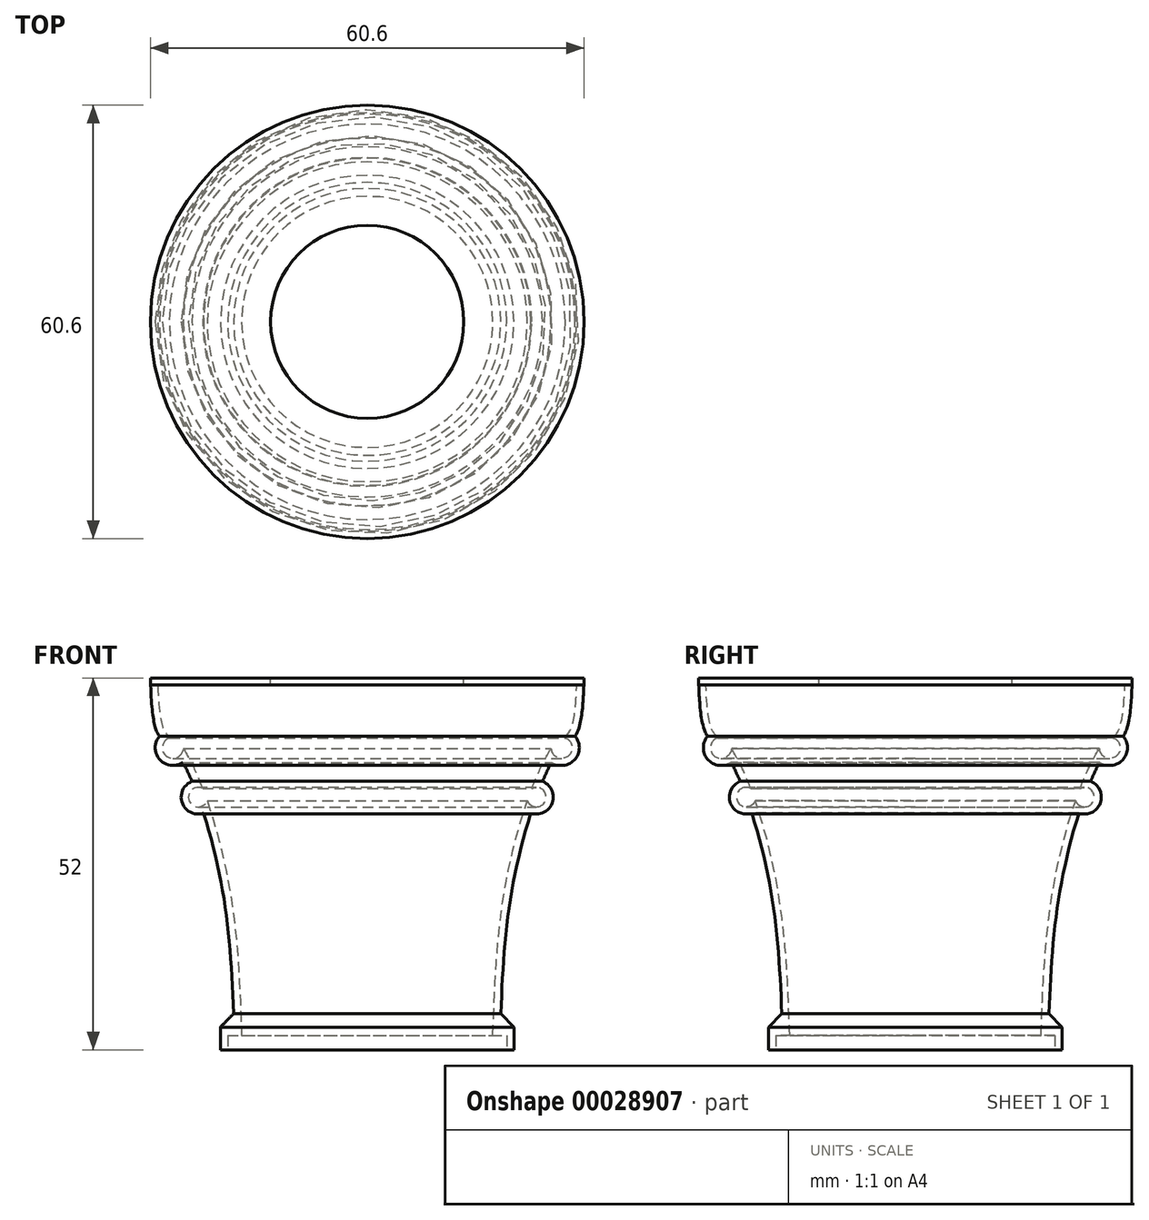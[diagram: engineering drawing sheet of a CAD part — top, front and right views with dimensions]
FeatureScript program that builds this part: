
annotation { "Feature Type Name" : "Feature", "Feature Type Description" : "" }
export const myFeature = defineFeature(function(context is Context, id is Id, definition is map)
    precondition{}
    {
        {
            var Q0;
            Q0=qCreatedBy(makeId("Front.planeOp"),FACE);
            var sketch = newSketch(context, id + "F0", { "sketchPlane" : qUnion([Q0])});
            skLineSegment(sketch, "E0", {"start": v(0, 0) * mm, "end": v(0, 52) * mm});
            skLineSegment(sketch, "E1", {"start": v(0, 52) * mm, "end": v(30.3, 52) * mm});
            skLineSegment(sketch, "E2", {"start": v(0, 0) * mm, "end": v(18.5, 0) * mm});
            skFitSpline(sketch, "E3", {"points": [v(30.3, 52) * mm, v(27.16, 42.24) * mm, v(21, 26.28) * mm, v(18.5, 0) * mm], "startDerivative": vector(-2.54, -110.8) * mm, "endDerivative": vector(-2.26, -73.48) * mm});
            skLineSegment(sketch, "E4.bottom", {"start": v(18.5, 0) * mm, "end": v(20.5, 0) * mm});
            skLineSegment(sketch, "E4.top", {"start": v(18.5, 3) * mm, "end": v(20.5, 3) * mm});
            skLineSegment(sketch, "E4.left", {"start": v(18.5, 0) * mm, "end": v(18.5, 3) * mm});
            skLineSegment(sketch, "E4.right", {"start": v(20.5, 0) * mm, "end": v(20.5, 3) * mm});
            skCircle(sketch, "E5", {"center": v(27.16, 42.24) * mm, "radius": 2.47 * mm});
            skCircle(sketch, "E6", {"center": v(23.63, 35.34) * mm, "radius": 2.36 * mm});
            skSolve(sketch);
        }
        {
            var Q0;
            Q0 = qSketchRegion(id + "F0", true);
            var Q1;
            Q1=sQuery(id+"F0.wireOp",EDGE,"E0");
            revolve(context, id + "F1", {"entities" : qUnion([Q0]), "axis" : qUnion([Q1]), "revolveType" : RevolveType.FULL});
        }
        {
            var Q0;
            Q0=makeQuery(id+"F1.opRevolve","SWEPT_FACE",FACE,{"disambiguationData":[OSD([sQuery(id+"F0.wireOp",EDGE,"E1")])]});
            var Q1;
            Q1=makeQuery(id+"F1.opRevolve","SWEPT_FACE",FACE,{"disambiguationData":[OSD([sQuery(id+"F0.wireOp",EDGE,"E2"),sQuery(id+"F0.wireOp",EDGE,"E4.bottom")])]});
            shell(context, id + "F2", {"entities" : qUnion([Q0, Q1]), "thickness" : 1 * mm});
        }
        {
            var Q0;
            Q0=makeQuery(id+"F1.opRevolve","SWEPT_FACE",FACE,{"disambiguationData":[OSD([sQuery(id+"F0.wireOp",EDGE,"E1")])]});
            var sketch = newSketch(context, id + "F3", { "sketchPlane" : qUnion([Q0])});
            skCircle(sketch, "E7.0", {"center": v(0, 0) * mm, "radius": 30.3 * mm});
            skCircle(sketch, "E8", {"center": v(0, 0) * mm, "radius": 13.5 * mm});
            skSolve(sketch);
        }
        {
            var Q0;
            Q0 = qSketchRegion(id + "F3", true);
            extrude(context, id + "F4", {"entities" : qUnion([Q0]), "operationType" : NewBodyOperationType.ADD, "oppositeDirection" : true, "depth" : 1 * mm});
        }
        {
            var Q0;
            Q0=makeQuery(id+"F1.opRevolve","SWEPT_EDGE",EDGE,{"disambiguationData":[OSD([sQuery(id+"F0.wireOp",EDGE,"E3"),sQuery(id+"F0.wireOp",EDGE,"E4.top")])]});
            chamfer(context, id + "F5", {"entities" : qUnion([Q0]), "width" : 2 * mm, "tangentPropagation" : true});
        }
    });
